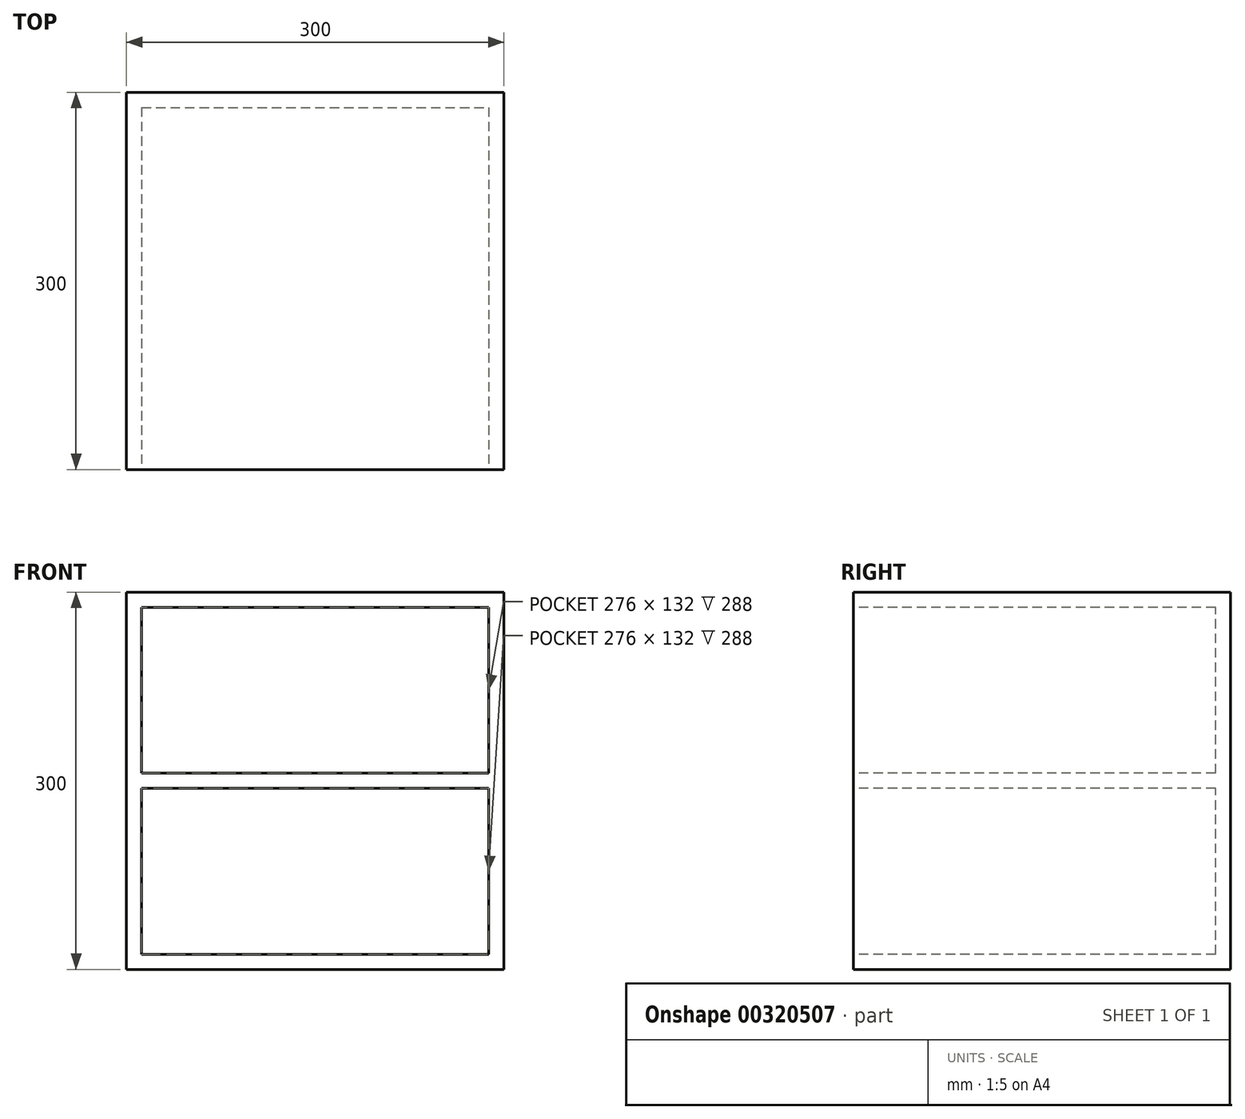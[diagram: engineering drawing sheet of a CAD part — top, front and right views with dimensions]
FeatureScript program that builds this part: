
annotation { "Feature Type Name" : "Feature", "Feature Type Description" : "" }
export const myFeature = defineFeature(function(context is Context, id is Id, definition is map)
    precondition{}
    {
        {
            var Q0;
            Q0=qCreatedBy(makeId("Front.planeOp"),FACE);
            var sketch = newSketch(context, id + "F0", { "sketchPlane" : qUnion([Q0])});
            skLineSegment(sketch, "E0.bottom", {"start": v(-150, -150) * mm, "end": v(150, -150) * mm});
            skLineSegment(sketch, "E0.top", {"start": v(-150, 150) * mm, "end": v(150, 150) * mm});
            skLineSegment(sketch, "E0.left", {"start": v(-150, -150) * mm, "end": v(-150, 150) * mm});
            skLineSegment(sketch, "E0.right", {"start": v(150, -150) * mm, "end": v(150, 150) * mm});
            skPoint(sketch, "E0.middle", {"position": v(0, 0) * mm});
            skSolve(sketch);
        }
        {
            var Q0;
            Q0=makeQuery(id+"F0.imprint","IMPRINT",FACE,{"disambiguationData":[TD([[makeQuery(id+"F0.imprint","IMPRINT",EDGE,{"derivedFrom":sQuery(id+"F0.wireOp",EDGE,"E0.bottom")}),1.0]])]});
            extrude(context, id + "F1", {"entities" : qUnion([Q0]), "oppositeDirection" : true, "depth" : 300 * mm});
        }
        {
            var Q0;
            Q0=makeQuery(id+"F1.opExtrude","CAP_FACE",FACE,{"disambiguationData":[OSD([sQuery(id+"F0.wireOp",EDGE,"E0.bottom"),sQuery(id+"F0.wireOp",EDGE,"E0.top"),sQuery(id+"F0.wireOp",EDGE,"E0.left"),sQuery(id+"F0.wireOp",EDGE,"E0.right")])],"isStart":true});
            shell(context, id + "F2", {"entities" : qUnion([Q0]), "thickness" : 12 * mm});
        }
        {
            var Q0;
            Q0=makeQuery(id+"F1.opExtrude","CAP_FACE",FACE,{"disambiguationData":[OSD([sQuery(id+"F0.wireOp",EDGE,"E0.bottom"),sQuery(id+"F0.wireOp",EDGE,"E0.top"),sQuery(id+"F0.wireOp",EDGE,"E0.left"),sQuery(id+"F0.wireOp",EDGE,"E0.right")])],"isStart":true});
            var sketch = newSketch(context, id + "F3", { "sketchPlane" : qUnion([Q0])});
            skLineSegment(sketch, "E1.bottom", {"start": v(-150, 6) * mm, "end": v(142.17, 6) * mm});
            skLineSegment(sketch, "E1.top", {"start": v(-150, -6) * mm, "end": v(142.17, -6) * mm});
            skLineSegment(sketch, "E1.left", {"start": v(-150, 6) * mm, "end": v(-150, -6) * mm});
            skLineSegment(sketch, "E1.right", {"start": v(142.17, 6) * mm, "end": v(142.17, -6) * mm});
            skPoint(sketch, "E1.middle", {"position": v(-3.92, 0) * mm});
            skSolve(sketch);
        }
        {
            var Q0;
            {var subQ0=sQuery(id+"F3.wireOp",EDGE,"E1.bottom");var subQ1=sQuery(id+"F0.wireOp",EDGE,"E0.left");var subQ2=makeQuery(id+"F2.opShell","OFFSET_EDGE",EDGE,{"disambiguationData":[OSD([subQ1]),TDD([makeQuery(id+"F1.opExtrude","CAP_EDGE",EDGE,{"disambiguationData":[OSD([subQ1])],"isStart":true})])]});var subQ3=makeQuery(id+"F3.imprint","INTERSECT",VERTEX,{"derivedFrom":[subQ2,subQ0]});Q0=makeQuery(id+"F3.imprint","IMPRINT",FACE,{"disambiguationData":[TD([[makeQuery(id+"F3.imprint","IMPRINT",EDGE,{"disambiguationData":[TD([[subQ3,-1.0]])],"derivedFrom":subQ0}),-1.0]])]});}
            extrude(context, id + "F4", {"entities" : qUnion([Q0]), "operationType" : NewBodyOperationType.ADD, "oppositeDirection" : true, "depth" : 295 * mm});
        }
    });
